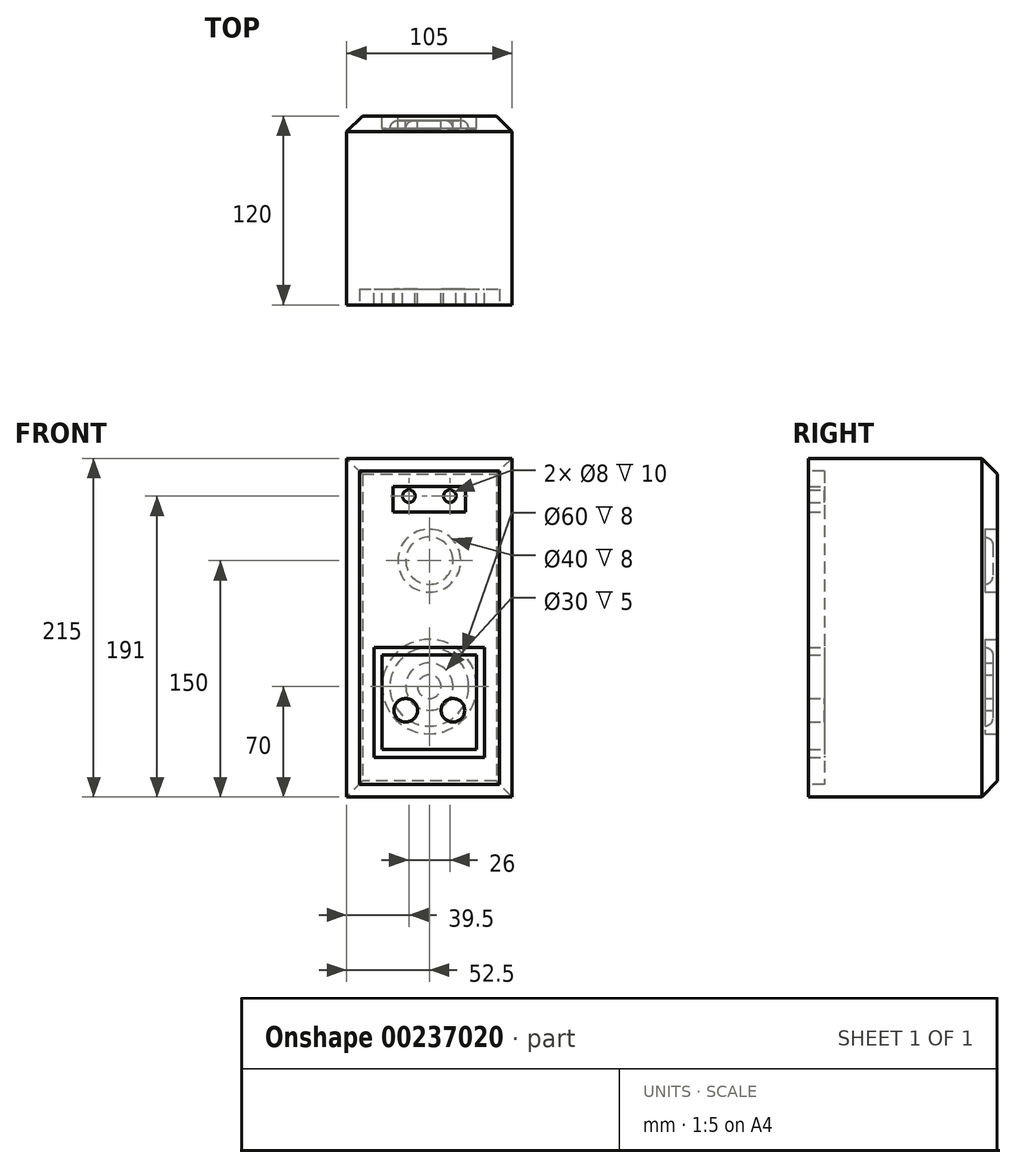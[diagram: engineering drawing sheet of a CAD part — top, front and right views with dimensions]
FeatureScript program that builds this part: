
annotation { "Feature Type Name" : "Feature", "Feature Type Description" : "" }
export const myFeature = defineFeature(function(context is Context, id is Id, definition is map)
    precondition{}
    {
        {
            var Q0;
            Q0=qCreatedBy(makeId("Top.planeOp"),FACE);
            var sketch = newSketch(context, id + "F0", { "sketchPlane" : qUnion([Q0])});
            skLineSegment(sketch, "E0.bottom", {"start": v(0, 0) * mm, "end": v(105, 0) * mm});
            skLineSegment(sketch, "E0.top", {"start": v(10, 120) * mm, "end": v(95, 120) * mm});
            skLineSegment(sketch, "E0.left", {"start": v(0, 0) * mm, "end": v(0, 110) * mm});
            skLineSegment(sketch, "E0.right", {"start": v(105, 0) * mm, "end": v(105, 110) * mm});
            skLineSegment(sketch, "E1", {"start": v(0, 110) * mm, "end": v(10, 120) * mm});
            skLineSegment(sketch, "E2", {"start": v(95, 120) * mm, "end": v(105, 110) * mm});
            skPoint(sketch, "E3.orphan", {"position": v(0, 120) * mm});
            skPoint(sketch, "E4.orphan", {"position": v(105, 120) * mm});
            skSolve(sketch);
        }
        {
            var Q0;
            Q0=makeQuery(id+"F0.imprint","IMPRINT",FACE,{"disambiguationData":[TD([[makeQuery(id+"F0.imprint","IMPRINT",EDGE,{"derivedFrom":sQuery(id+"F0.wireOp",EDGE,"E0.bottom")}),1.0]])]});
            extrude(context, id + "F1", {"entities" : qUnion([Q0]), "depth" : 215 * mm});
        }
        {
            var Q0;
            Q0=makeQuery(id+"F1.opExtrude","CAP_EDGE",EDGE,{"disambiguationData":[OSD([sQuery(id+"F0.wireOp",EDGE,"E0.top")])],"isStart":false});
            var Q1;
            Q1=makeQuery(id+"F1.opExtrude","CAP_EDGE",EDGE,{"disambiguationData":[OSD([sQuery(id+"F0.wireOp",EDGE,"E0.top")])],"isStart":true});
            chamfer(context, id + "F2", {"entities" : qUnion([Q0, Q1]), "width" : 10 * mm, "tangentPropagation" : true});
        }
        {
            var Q0;
            Q0=makeQuery(id+"F1.opExtrude","SWEPT_FACE",FACE,{"disambiguationData":[OSD([sQuery(id+"F0.wireOp",EDGE,"E0.top")])]});
            var sketch = newSketch(context, id + "F3", { "sketchPlane" : qUnion([Q0])});
            skCircle(sketch, "E5", {"center": v(-52.5, 150) * mm, "radius": 20 * mm});
            skCircle(sketch, "E6", {"center": v(-52.5, 70) * mm, "radius": 30 * mm});
            skSolve(sketch);
        }
        {
            var Q0;
            Q0=makeQuery(id+"F3.imprint","IMPRINT",FACE,{"disambiguationData":[TD([[makeQuery(id+"F3.imprint","IMPRINT",EDGE,{"derivedFrom":sQuery(id+"F3.wireOp",EDGE,"E5")}),1.0]])]});
            var Q1;
            Q1=makeQuery(id+"F3.imprint","IMPRINT",FACE,{"disambiguationData":[TD([[makeQuery(id+"F3.imprint","IMPRINT",EDGE,{"derivedFrom":sQuery(id+"F3.wireOp",EDGE,"E6")}),1.0]])]});
            extrude(context, id + "F4", {"entities" : qUnion([Q0, Q1]), "operationType" : NewBodyOperationType.REMOVE, "oppositeDirection" : true, "depth" : 8 * mm});
        }
        {
            var Q0;
            Q0=makeQuery(id+"F4.boolean.opBoolean","COPY",FACE,{"derivedFrom":makeQuery(id+"F4.opExtrude","CAP_FACE",FACE,{"disambiguationData":[OSD([sQuery(id+"F3.wireOp",EDGE,"E5")])],"isStart":false})});
            var sketch = newSketch(context, id + "F5", { "sketchPlane" : qUnion([Q0])});
            skCircle(sketch, "E7", {"center": v(-52.5, 150) * mm, "radius": 15 * mm});
            skCircle(sketch, "E8", {"center": v(-52.5, 70) * mm, "radius": 25 * mm});
            skSolve(sketch);
        }
        {
            var Q0;
            Q0=makeQuery(id+"F5.imprint","IMPRINT",FACE,{"disambiguationData":[TD([[makeQuery(id+"F5.imprint","IMPRINT",EDGE,{"derivedFrom":sQuery(id+"F5.wireOp",EDGE,"E7")}),1.0]])]});
            var Q1;
            Q1=makeQuery(id+"F5.imprint","IMPRINT",FACE,{"disambiguationData":[TD([[makeQuery(id+"F5.imprint","IMPRINT",EDGE,{"derivedFrom":sQuery(id+"F5.wireOp",EDGE,"E8")}),1.0]])]});
            extrude(context, id + "F6", {"entities" : qUnion([Q0, Q1]), "operationType" : NewBodyOperationType.ADD, "depth" : 5 * mm});
        }
        {
            var Q0;
            Q0=makeQuery(id+"F6.opExtrude","CAP_EDGE",EDGE,{"disambiguationData":[OSD([sQuery(id+"F5.wireOp",EDGE,"E8")])],"isStart":false});
            var Q1;
            Q1=makeQuery(id+"F6.opExtrude","CAP_EDGE",EDGE,{"disambiguationData":[OSD([sQuery(id+"F5.wireOp",EDGE,"E7")])],"isStart":false});
            fillet(context, id + "F7", {"entities" : qUnion([Q0, Q1]), "radius" : 5 * mm, "tangentPropagation" : true, "allowEdgeOverflow" : false});
        }
        {
            var Q0;
            Q0=makeQuery(id+"F6.opExtrude","CAP_FACE",FACE,{"disambiguationData":[OSD([sQuery(id+"F5.wireOp",EDGE,"E8")])],"isStart":false});
            var sketch = newSketch(context, id + "F8", { "sketchPlane" : qUnion([Q0])});
            skCircle(sketch, "E9", {"center": v(-52.5, 70) * mm, "radius": 15 * mm});
            skCircle(sketch, "E10", {"center": v(-52.5, 70) * mm, "radius": 7.5 * mm});
            skSolve(sketch);
        }
        {
            var Q0;
            Q0=makeQuery(id+"F8.imprint","IMPRINT",FACE,{"disambiguationData":[TD([[makeQuery(id+"F8.imprint","IMPRINT",EDGE,{"derivedFrom":sQuery(id+"F8.wireOp",EDGE,"E9")}),1.0]])]});
            extrude(context, id + "F9", {"entities" : qUnion([Q0]), "operationType" : NewBodyOperationType.REMOVE, "oppositeDirection" : true, "depth" : 5 * mm});
        }
        {
            var Q0;
            Q0=makeQuery(id+"F1.opExtrude","SWEPT_FACE",FACE,{"disambiguationData":[OSD([sQuery(id+"F0.wireOp",EDGE,"E0.bottom")])]});
            var sketch = newSketch(context, id + "F10", { "sketchPlane" : qUnion([Q0])});
            skLineSegment(sketch, "E11.bottom", {"start": v(8, 207) * mm, "end": v(97, 207) * mm});
            skLineSegment(sketch, "E11.top", {"start": v(8, 8) * mm, "end": v(97, 8) * mm});
            skLineSegment(sketch, "E11.left", {"start": v(8, 207) * mm, "end": v(8, 8) * mm});
            skLineSegment(sketch, "E11.right", {"start": v(97, 207) * mm, "end": v(97, 8) * mm});
            skSolve(sketch);
        }
        {
            var Q0;
            Q0=makeQuery(id+"F10.imprint","IMPRINT",FACE,{"disambiguationData":[TD([[makeQuery(id+"F10.imprint","IMPRINT",EDGE,{"derivedFrom":sQuery(id+"F10.wireOp",EDGE,"E11.bottom")}),-1.0]])]});
            extrude(context, id + "F11", {"entities" : qUnion([Q0]), "operationType" : NewBodyOperationType.REMOVE, "oppositeDirection" : true, "depth" : 10 * mm});
        }
        {
            var Q0;
            Q0=makeQuery(id+"F11.boolean.opBoolean","COPY",FACE,{"derivedFrom":makeQuery(id+"F11.opExtrude","CAP_FACE",FACE,{"disambiguationData":[OSD([sQuery(id+"F10.wireOp",EDGE,"E11.bottom"),sQuery(id+"F10.wireOp",EDGE,"E11.top"),sQuery(id+"F10.wireOp",EDGE,"E11.left"),sQuery(id+"F10.wireOp",EDGE,"E11.right")])],"isStart":false})});
            var sketch = newSketch(context, id + "F12", { "sketchPlane" : qUnion([Q0])});
            skLineSegment(sketch, "E12.bottom", {"start": v(29.5, 197) * mm, "end": v(75.5, 197) * mm});
            skLineSegment(sketch, "E12.top", {"start": v(29.5, 181) * mm, "end": v(75.5, 181) * mm});
            skLineSegment(sketch, "E12.left", {"start": v(29.5, 197) * mm, "end": v(29.5, 181) * mm});
            skLineSegment(sketch, "E12.right", {"start": v(75.5, 197) * mm, "end": v(75.5, 181) * mm});
            skCircle(sketch, "E13", {"center": v(39.5, 191) * mm, "radius": 4 * mm});
            skCircle(sketch, "E14", {"center": v(65.5, 191) * mm, "radius": 4 * mm});
            skSolve(sketch);
        }
        {
            var Q0;
            Q0=makeQuery(id+"F12.imprint","IMPRINT",FACE,{"disambiguationData":[TD([[makeQuery(id+"F12.imprint","IMPRINT",EDGE,{"derivedFrom":sQuery(id+"F12.wireOp",EDGE,"E12.bottom")}),-1.0]])]});
            extrude(context, id + "F13", {"entities" : qUnion([Q0]), "operationType" : NewBodyOperationType.ADD, "depth" : 10 * mm});
        }
        {
            var Q0;
            {var subQ0=sQuery(id+"F10.wireOp",EDGE,"E11.left");var subQ1=sQuery(id+"F10.wireOp",EDGE,"E11.right");var subQ2=sQuery(id+"F10.wireOp",EDGE,"E11.top");var subQ3=sQuery(id+"F10.wireOp",EDGE,"E11.bottom");Q0=makeQuery(id+"F13.boolean.opBoolean","SPLIT",FACE,{"disambiguationData":[TD([makeQuery(id+"F11.boolean.opBoolean","COPY",FACE,{"derivedFrom":makeQuery(id+"F11.opExtrude","SWEPT_FACE",FACE,{"disambiguationData":[OSD([subQ3])]})})])],"derivedFrom":makeQuery(id+"F11.boolean.opBoolean","COPY",FACE,{"derivedFrom":makeQuery(id+"F11.opExtrude","CAP_FACE",FACE,{"disambiguationData":[OSD([subQ3,subQ2,subQ0,subQ1])],"isStart":false})})});}
            var sketch = newSketch(context, id + "F14", { "sketchPlane" : qUnion([Q0])});
            skLineSegment(sketch, "E15.bottom", {"start": v(17.5, 95) * mm, "end": v(87.5, 95) * mm});
            skLineSegment(sketch, "E15.top", {"start": v(17.5, 25) * mm, "end": v(87.5, 25) * mm});
            skLineSegment(sketch, "E15.left", {"start": v(17.5, 95) * mm, "end": v(17.5, 25) * mm});
            skLineSegment(sketch, "E15.right", {"start": v(87.5, 95) * mm, "end": v(87.5, 25) * mm});
            skLineSegment(sketch, "E16.bottom", {"start": v(22.5, 90) * mm, "end": v(82.5, 90) * mm});
            skLineSegment(sketch, "E16.top", {"start": v(22.5, 30) * mm, "end": v(82.5, 30) * mm});
            skLineSegment(sketch, "E16.left", {"start": v(22.5, 90) * mm, "end": v(22.5, 30) * mm});
            skLineSegment(sketch, "E16.right", {"start": v(82.5, 90) * mm, "end": v(82.5, 30) * mm});
            skCircle(sketch, "E17", {"center": v(37.5, 55) * mm, "radius": 7.5 * mm});
            skCircle(sketch, "E18", {"center": v(67.5, 55) * mm, "radius": 7.5 * mm});
            skSolve(sketch);
        }
        {
            var Q0;
            Q0=makeQuery(id+"F14.imprint","IMPRINT",FACE,{"disambiguationData":[TD([[makeQuery(id+"F14.imprint","IMPRINT",EDGE,{"derivedFrom":sQuery(id+"F14.wireOp",EDGE,"E15.bottom")}),-1.0]])]});
            var Q1;
            Q1=makeQuery(id+"F14.imprint","IMPRINT",FACE,{"disambiguationData":[TD([[makeQuery(id+"F14.imprint","IMPRINT",EDGE,{"derivedFrom":sQuery(id+"F14.wireOp",EDGE,"E18")}),1.0]])]});
            var Q2;
            Q2=makeQuery(id+"F14.imprint","IMPRINT",FACE,{"disambiguationData":[TD([[makeQuery(id+"F14.imprint","IMPRINT",EDGE,{"derivedFrom":sQuery(id+"F14.wireOp",EDGE,"E17")}),1.0]])]});
            extrude(context, id + "F15", {"entities" : qUnion([Q0, Q1, Q2]), "operationType" : NewBodyOperationType.ADD, "depth" : 10 * mm});
        }
    });
